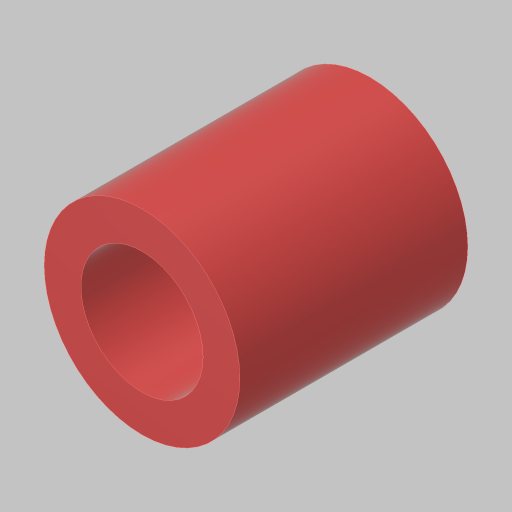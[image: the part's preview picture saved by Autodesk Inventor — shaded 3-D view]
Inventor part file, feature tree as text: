
AUTODESK INVENTOR PART (.ipt)
format: ipt  version: 2023.5 (Build 275446000, 446)  size: 115,200 bytes
history: native  units: in
note: dims shown in document units (in); Inventor stores cm internally (conversion verified against a paired STEP export)
features: extrude x1, sketch x1
ambient origin geometry x8: Origin, YZ Plane, XZ Plane, XY Plane, X Axis, Y Axis, Z Axis, Center Point
bodies: Solid1 (feature_tree)
feature tree (2):
  extrude  "Extrusion1"  Depth=0.7745in
  sketch  "Sketch1"  dims[d0=0.125in d1=0.415in d2=0.7745in d3=0.0in]
